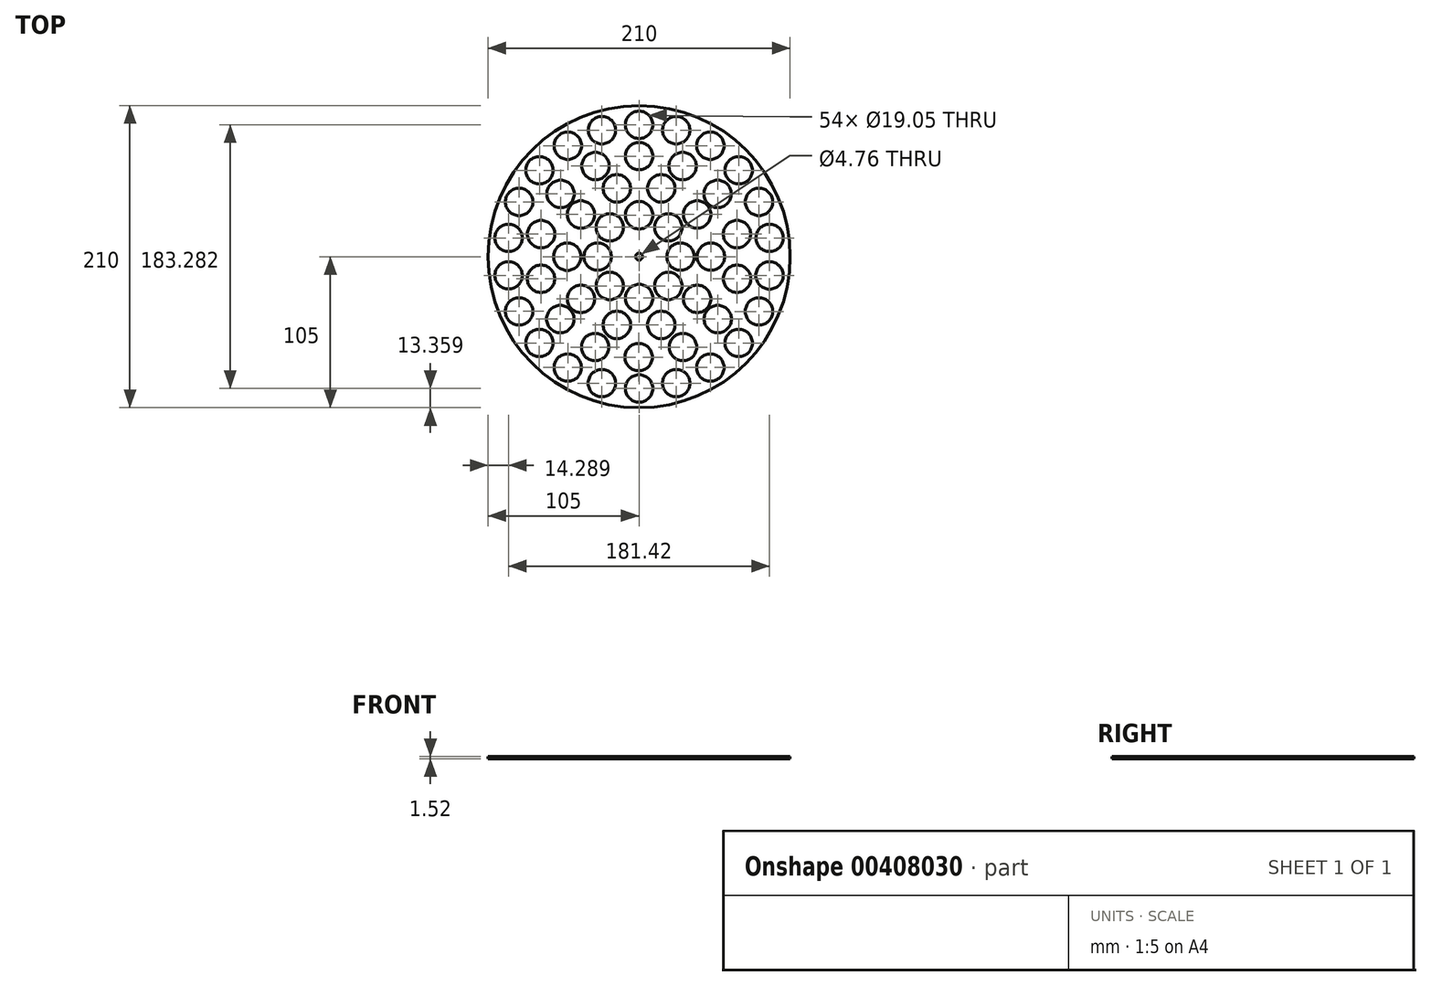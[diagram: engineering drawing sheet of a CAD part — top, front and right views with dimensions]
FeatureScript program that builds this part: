
annotation { "Feature Type Name" : "Feature", "Feature Type Description" : "" }
export const myFeature = defineFeature(function(context is Context, id is Id, definition is map)
    precondition{}
    {
        {
            var Q0;
            Q0=qCreatedBy(makeId("Top.planeOp"),FACE);
            var sketch = newSketch(context, id + "F0", { "sketchPlane" : qUnion([Q0])});
            skCircle(sketch, "E0", {"center": v(0, 0) * mm, "radius": 105 * mm});
            skCircle(sketch, "E1", {"center": v(0, 0) * mm, "radius": 40 * mm, "construction": true});
            skCircle(sketch, "E2", {"center": v(0, 28.8) * mm, "radius": 9.53 * mm});
            skCircle(sketch, "E3", {"center": v(54.73, -43.4) * mm, "radius": 9.53 * mm});
            skCircle(sketch, "E4", {"center": v(-69.27, -60) * mm, "radius": 9.53 * mm});
            skCircle(sketch, "E5", {"center": v(-83.37, -38.05) * mm, "radius": 9.53 * mm});
            skCircle(sketch, "E6", {"center": v(-30.52, -62.83) * mm, "radius": 9.53 * mm});
            skCircle(sketch, "E7", {"center": v(-49.56, -77.08) * mm, "radius": 9.53 * mm});
            skCircle(sketch, "E8", {"center": v(-25.8, 87.93) * mm, "radius": 9.53 * mm});
            skCircle(sketch, "E9", {"center": v(49.55, 77.09) * mm, "radius": 9.53 * mm});
            skCircle(sketch, "E10", {"center": v(-0.27, -69.85) * mm, "radius": 9.53 * mm});
            skCircle(sketch, "E11", {"center": v(30.52, -62.83) * mm, "radius": 9.53 * mm});
            skCircle(sketch, "E12", {"center": v(90.7, -13.05) * mm, "radius": 9.53 * mm});
            skCircle(sketch, "E13", {"center": v(90.7, 13.04) * mm, "radius": 9.53 * mm});
            skCircle(sketch, "E14", {"center": v(20.36, 20.36) * mm, "radius": 9.53 * mm});
            skCircle(sketch, "E15", {"center": v(-90.71, -13.03) * mm, "radius": 9.53 * mm});
            skCircle(sketch, "E16", {"center": v(-90.7, 13.06) * mm, "radius": 9.53 * mm});
            skCircle(sketch, "E17", {"center": v(-83.35, 38.08) * mm, "radius": 9.53 * mm});
            skCircle(sketch, "E18", {"center": v(69.26, 60) * mm, "radius": 9.53 * mm});
            skCircle(sketch, "E19", {"center": v(83.36, 38.06) * mm, "radius": 9.53 * mm});
            skCircle(sketch, "E20", {"center": v(-54.73, -43.4) * mm, "radius": 9.53 * mm});
            skCircle(sketch, "E21", {"center": v(-49.53, 77.1) * mm, "radius": 9.53 * mm});
            skCircle(sketch, "E22", {"center": v(-69.25, 60.02) * mm, "radius": 9.53 * mm});
            skCircle(sketch, "E23", {"center": v(25.83, 87.93) * mm, "radius": 9.53 * mm});
            skCircle(sketch, "E24", {"center": v(-28.8, 0) * mm, "radius": 9.53 * mm});
            skCircle(sketch, "E25", {"center": v(20.36, -20.36) * mm, "radius": 9.53 * mm});
            skCircle(sketch, "E26", {"center": v(-20.36, -20.36) * mm, "radius": 9.53 * mm});
            skCircle(sketch, "E27", {"center": v(-20.36, 20.36) * mm, "radius": 9.53 * mm});
            skCircle(sketch, "E28", {"center": v(0.01, 91.64) * mm, "radius": 9.53 * mm});
            skCircle(sketch, "E29", {"center": v(54.56, 43.61) * mm, "radius": 9.53 * mm});
            skCircle(sketch, "E30", {"center": v(0, 69.85) * mm, "radius": 9.53 * mm});
            skCircle(sketch, "E31", {"center": v(68.13, -15.4) * mm, "radius": 9.53 * mm});
            skCircle(sketch, "E32", {"center": v(68.07, 15.66) * mm, "radius": 9.53 * mm});
            skCircle(sketch, "E33", {"center": v(30.27, 62.95) * mm, "radius": 9.53 * mm});
            skCircle(sketch, "E34", {"center": v(0, -28.8) * mm, "radius": 9.53 * mm});
            skCircle(sketch, "E35", {"center": v(28.8, 0) * mm, "radius": 9.53 * mm});
            skCircle(sketch, "E36", {"center": v(0, 0) * mm, "radius": 2.38 * mm});
            skCircle(sketch, "E37", {"center": v(0, 0) * mm, "radius": 28.8 * mm, "construction": true});
            skCircle(sketch, "E38", {"center": v(0, 0) * mm, "radius": 69.85 * mm, "construction": true});
            skCircle(sketch, "E39", {"center": v(0, 0) * mm, "radius": 91.64 * mm, "construction": true});
            skCircle(sketch, "E40", {"center": v(0, 0) * mm, "radius": 80 * mm, "construction": true});
            skCircle(sketch, "E41", {"center": v(83.36, -38.07) * mm, "radius": 9.53 * mm});
            skCircle(sketch, "E42", {"center": v(69.26, -60.01) * mm, "radius": 9.53 * mm});
            skCircle(sketch, "E43", {"center": v(40.38, 29.33) * mm, "radius": 9.53 * mm});
            skCircle(sketch, "E44", {"center": v(49.91, 0) * mm, "radius": 9.53 * mm});
            skCircle(sketch, "E45", {"center": v(-15.41, -47.47) * mm, "radius": 9.53 * mm});
            skCircle(sketch, "E46", {"center": v(-49.91, -0.02) * mm, "radius": 9.53 * mm});
            skCircle(sketch, "E47", {"center": v(-40.4, 29.32) * mm, "radius": 9.53 * mm});
            skCircle(sketch, "E48", {"center": v(15.43, -47.47) * mm, "radius": 9.53 * mm});
            skCircle(sketch, "E49", {"center": v(40.38, -29.33) * mm, "radius": 9.53 * mm});
            skCircle(sketch, "E50", {"center": v(-15.45, 47.46) * mm, "radius": 9.53 * mm});
            skCircle(sketch, "E51", {"center": v(15.43, 47.47) * mm, "radius": 9.53 * mm});
            skCircle(sketch, "E52", {"center": v(0, 0) * mm, "radius": 49.91 * mm, "construction": true});
            skCircle(sketch, "E53", {"center": v(-40.37, -29.35) * mm, "radius": 9.53 * mm});
            skCircle(sketch, "E54", {"center": v(-30.27, 62.95) * mm, "radius": 9.53 * mm});
            skCircle(sketch, "E55", {"center": v(-68.13, -15.4) * mm, "radius": 9.53 * mm});
            skCircle(sketch, "E56", {"center": v(-25.82, -87.93) * mm, "radius": 9.53 * mm});
            skCircle(sketch, "E57", {"center": v(-54.56, 43.61) * mm, "radius": 9.53 * mm});
            skCircle(sketch, "E58", {"center": v(-68.07, 15.66) * mm, "radius": 9.53 * mm});
            skCircle(sketch, "E59", {"center": v(0, -91.64) * mm, "radius": 9.53 * mm});
            skCircle(sketch, "E60", {"center": v(25.82, -87.93) * mm, "radius": 9.53 * mm});
            skCircle(sketch, "E61", {"center": v(49.54, -77.1) * mm, "radius": 9.53 * mm});
            skSolve(sketch);
        }
        {
            var Q0;
            Q0=makeQuery(id+"F0.imprint","IMPRINT",FACE,{"disambiguationData":[TD([[makeQuery(id+"F0.imprint","IMPRINT",EDGE,{"derivedFrom":sQuery(id+"F0.wireOp",EDGE,"E2")}),-1.0]])]});
            extrude(context, id + "F1", {"entities" : qUnion([Q0]), "depth" : 1.52 * mm, "offsetDistance" : 25.4 * mm});
        }
    });
